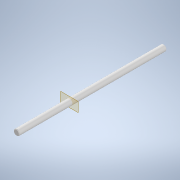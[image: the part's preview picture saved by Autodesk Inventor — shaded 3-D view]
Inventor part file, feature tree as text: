
AUTODESK INVENTOR PART (.ipt)
format: ipt  version: 2021 (Build 250183000, 183)  size: 100,864 bytes
history: native  units: mm
features: other x4, extrude x1, chamfer x1, sketch x1, reference x1
ambient origin geometry x8: Origin, YZ Plane, XZ Plane, XY Plane, X Axis, Y Axis, Z Axis, Center Point
bodies: Body1 (feature_tree)
feature tree (8):
  other  "Bryła1"
  other  "Płaszczyzna konstrukcyjna1"
  extrude  "Wyciągnięcie proste1"  Depth=20.0mm
  chamfer  "Faza1"  Distance=180.0mm
  sketch  "Szkic1"
  reference  "Odniesienie1"
  other  "zespul12_2.iam"
  other  "shaft:1"
